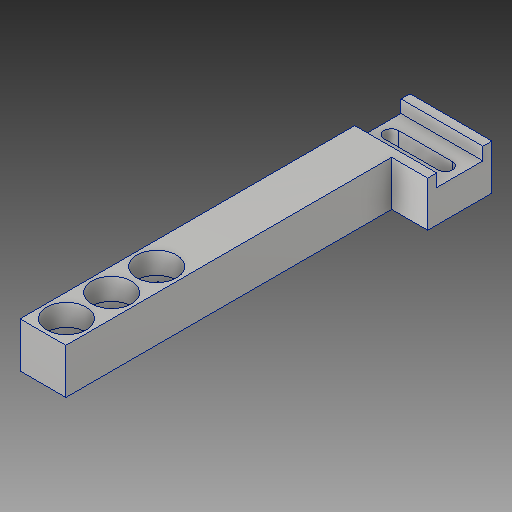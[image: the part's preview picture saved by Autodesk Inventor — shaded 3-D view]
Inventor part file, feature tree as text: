
AUTODESK INVENTOR PART (.ipt)
format: ipt  version: 2019 (Build 230136000, 136)  size: 153,600 bytes
history: native  units: mm
features: extrude x5, sketch x4
ambient origin geometry x8: Origin, YZ Plane, XZ Plane, XY Plane, X Axis, Y Axis, Z Axis, Center Point
bodies: Solid1 (feature_tree)
feature tree (9):
  extrude  "Extrusion1"  Depth=108.0mm
  extrude  "Extrusion2"  Depth=90.2mm
  extrude  "Extrusion3"  Depth=12.8mm
  sketch  "Sketch4"  dims[d7=3.5mm d8=0.0mm d9=4.0mm d10=4.0mm d11=3.5mm d12=0.0mm d13=11.0mm d14=11.0mm d15=11.0mm d16=12.5mm d17=12.5mm d18=6.5mm d19=6.5mm d20=6.5mm d21=3.5mm d22=0.0mm d23=6.0mm d24=0.0mm d25=6.5mm d26=15.0mm d27=4.0mm]
  extrude  "Extrusion4"  Depth=4.0mm
  extrude  "Extrusion5"  Depth=4.0mm
  sketch  "Sketch1"  dims[d0=22.7mm d1=108.0mm]
  sketch  "Sketch2"  dims[d2=12.7mm d3=90.2mm]
  sketch  "Sketch3"  dims[d4=12.5mm d5=0.0mm d6=12.8mm]
